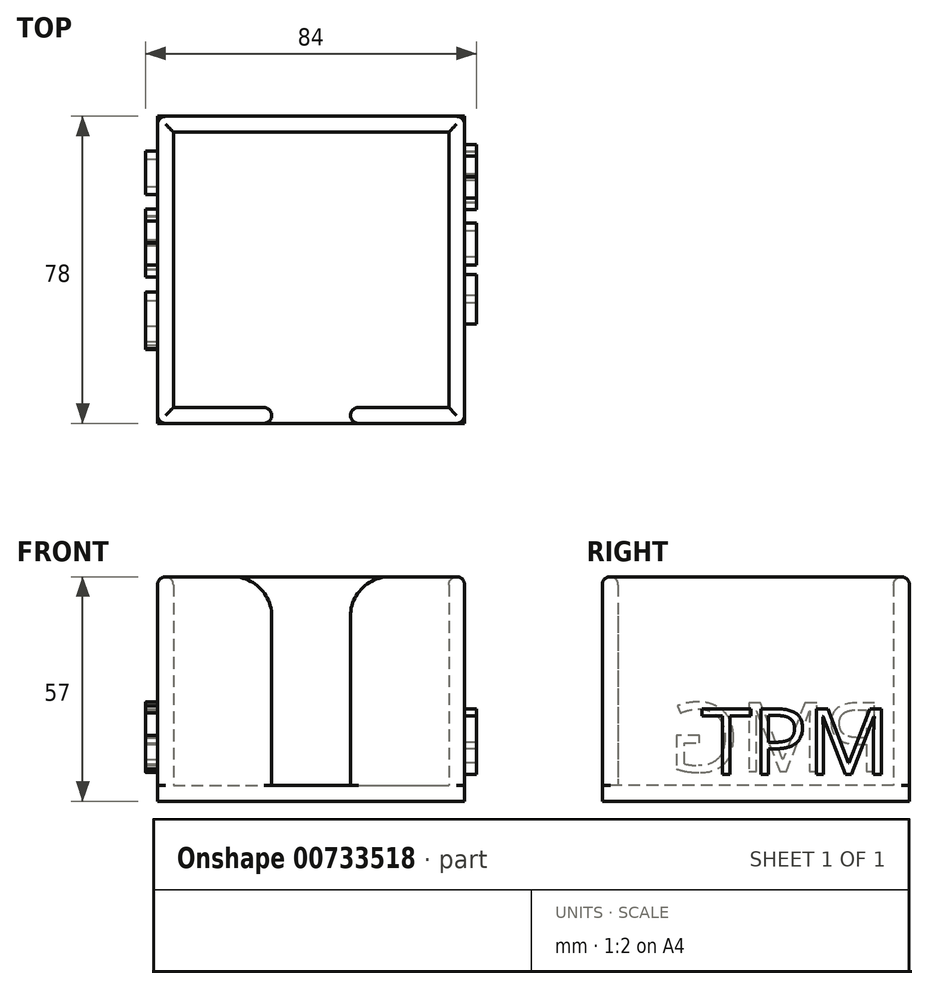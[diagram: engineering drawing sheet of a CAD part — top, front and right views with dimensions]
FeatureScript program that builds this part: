
annotation { "Feature Type Name" : "Feature", "Feature Type Description" : "" }
export const myFeature = defineFeature(function(context is Context, id is Id, definition is map)
    precondition{}
    {
        {
            var Q0;
            Q0=qCreatedBy(makeId("Top.planeOp"),FACE);
            var sketch = newSketch(context, id + "F0", { "sketchPlane" : qUnion([Q0])});
            skLineSegment(sketch, "E0.bottom", {"start": v(0, 0) * mm, "end": v(78, 0) * mm});
            skLineSegment(sketch, "E0.top", {"start": v(0, -78) * mm, "end": v(29, -78) * mm});
            skLineSegment(sketch, "E0.left", {"start": v(0, 0) * mm, "end": v(0, -78) * mm});
            skLineSegment(sketch, "E0.right", {"start": v(78, 0) * mm, "end": v(78, -78) * mm});
            skLineSegment(sketch, "E1.bottom", {"start": v(4, -4) * mm, "end": v(74, -4) * mm});
            skLineSegment(sketch, "E1.top", {"start": v(4, -74) * mm, "end": v(29, -74) * mm});
            skLineSegment(sketch, "E1.left", {"start": v(4, -4) * mm, "end": v(4, -74) * mm});
            skLineSegment(sketch, "E1.right", {"start": v(74, -4) * mm, "end": v(74, -74) * mm});
            skLineSegment(sketch, "E2", {"start": v(29, -74) * mm, "end": v(29, -78) * mm});
            skLineSegment(sketch, "E3", {"start": v(49, -74) * mm, "end": v(49, -78) * mm});
            skLineSegment(sketch, "E4.trimOffspring", {"start": v(49, -74) * mm, "end": v(74, -74) * mm});
            skLineSegment(sketch, "E5.trimOffspring", {"start": v(49, -78) * mm, "end": v(78, -78) * mm});
            skSolve(sketch);
        }
        {
            var Q0;
            Q0 = qSketchRegion(id + "F0", true);
            extrude(context, id + "F1", {"entities" : qUnion([Q0]), "depth" : 57 * mm, "offsetDistance" : 25 * mm});
        }
        {
            var Q0;
            Q0=makeQuery(id+"F1.opExtrude","CAP_EDGE",EDGE,{"disambiguationData":[OSD([sQuery(id+"F0.wireOp",EDGE,"E2")])],"isStart":false});
            var Q1;
            Q1=makeQuery(id+"F1.opExtrude","CAP_EDGE",EDGE,{"disambiguationData":[OSD([sQuery(id+"F0.wireOp",EDGE,"E3")])],"isStart":false});
            fillet(context, id + "F2", {"entities" : qUnion([Q0, Q1]), "radius" : 10 * mm, "tangentPropagation" : true, "allowEdgeOverflow" : false});
        }
        {
            var Q0;
            Q0=makeQuery(id+"F1.opExtrude","CAP_EDGE",EDGE,{"disambiguationData":[OSD([sQuery(id+"F0.wireOp",EDGE,"E0.top")])],"isStart":false});
            var Q1;
            Q1=makeQuery(id+"F1.opExtrude","CAP_EDGE",EDGE,{"disambiguationData":[OSD([sQuery(id+"F0.wireOp",EDGE,"E1.top")])],"isStart":false});
            var Q2;
            Q2=makeQuery(id+"F1.opExtrude","CAP_EDGE",EDGE,{"disambiguationData":[OSD([sQuery(id+"F0.wireOp",EDGE,"E1.left")])],"isStart":false});
            var Q3;
            Q3=makeQuery(id+"F1.opExtrude","CAP_EDGE",EDGE,{"disambiguationData":[OSD([sQuery(id+"F0.wireOp",EDGE,"E0.left")])],"isStart":false});
            var Q4;
            Q4=makeQuery(id+"F1.opExtrude","CAP_EDGE",EDGE,{"disambiguationData":[OSD([sQuery(id+"F0.wireOp",EDGE,"E1.bottom")])],"isStart":false});
            var Q5;
            Q5=makeQuery(id+"F1.opExtrude","CAP_EDGE",EDGE,{"disambiguationData":[OSD([sQuery(id+"F0.wireOp",EDGE,"E0.bottom")])],"isStart":false});
            var Q6;
            Q6=makeQuery(id+"F1.opExtrude","CAP_EDGE",EDGE,{"disambiguationData":[OSD([sQuery(id+"F0.wireOp",EDGE,"E0.right")])],"isStart":false});
            var Q7;
            Q7=makeQuery(id+"F1.opExtrude","CAP_EDGE",EDGE,{"disambiguationData":[OSD([sQuery(id+"F0.wireOp",EDGE,"E1.right")])],"isStart":false});
            var Q8;
            Q8=makeQuery(id+"F1.opExtrude","CAP_EDGE",EDGE,{"disambiguationData":[OSD([sQuery(id+"F0.wireOp",EDGE,"E4.trimOffspring")])],"isStart":false});
            var Q9;
            Q9=makeQuery(id+"F1.opExtrude","CAP_EDGE",EDGE,{"disambiguationData":[OSD([sQuery(id+"F0.wireOp",EDGE,"E5.trimOffspring")])],"isStart":false});
            var Q10;
            Q10=makeQuery(id+"F1.opExtrude","SWEPT_EDGE",EDGE,{"disambiguationData":[OSD([sQuery(id+"F0.wireOp",EDGE,"E0.top"),sQuery(id+"F0.wireOp",EDGE,"E0.left")])]});
            var Q11;
            Q11=makeQuery(id+"F1.opExtrude","SWEPT_EDGE",EDGE,{"disambiguationData":[OSD([sQuery(id+"F0.wireOp",EDGE,"E0.bottom"),sQuery(id+"F0.wireOp",EDGE,"E0.right")])]});
            var Q12;
            Q12=makeQuery(id+"F1.opExtrude","SWEPT_EDGE",EDGE,{"disambiguationData":[OSD([sQuery(id+"F0.wireOp",EDGE,"E0.right"),sQuery(id+"F0.wireOp",EDGE,"E5.trimOffspring")])]});
            var Q13;
            Q13=makeQuery(id+"F1.opExtrude","SWEPT_EDGE",EDGE,{"disambiguationData":[OSD([sQuery(id+"F0.wireOp",EDGE,"E0.bottom"),sQuery(id+"F0.wireOp",EDGE,"E0.left")])]});
            fillet(context, id + "F3", {"entities" : qUnion([Q0, Q1, Q2, Q3, Q4, Q5, Q6, Q7, Q8, Q9, Q10, Q11, Q12, Q13]), "radius" : 2 * mm, "tangentPropagation" : true, "allowEdgeOverflow" : false});
        }
        {
            var Q0;
            Q0=qCreatedBy(makeId("Top.planeOp"),FACE);
            var sketch = newSketch(context, id + "F4", { "sketchPlane" : qUnion([Q0])});
            skLineSegment(sketch, "E6.bottom", {"start": v(0, 0) * mm, "end": v(78, 0) * mm});
            skLineSegment(sketch, "E6.top", {"start": v(0, -78) * mm, "end": v(78, -78) * mm});
            skLineSegment(sketch, "E6.left", {"start": v(0, 0) * mm, "end": v(0, -78) * mm});
            skLineSegment(sketch, "E6.right", {"start": v(78, 0) * mm, "end": v(78, -78) * mm});
            skSolve(sketch);
        }
        {
            var Q0;
            Q0 = qSketchRegion(id + "F4", true);
            extrude(context, id + "F5", {"entities" : qUnion([Q0]), "operationType" : NewBodyOperationType.ADD, "depth" : 4 * mm, "offsetDistance" : 25 * mm});
        }
        {
            var Q0;
            Q0=makeQuery(id+"F5.boolean.opBoolean","MERGE",FACE,{"derivedFrom":[makeQuery(id+"F1.opExtrude","SWEPT_FACE",FACE,{"disambiguationData":[OSD([sQuery(id+"F0.wireOp",EDGE,"E0.right")])]}),makeQuery(id+"F5.opExtrude","SWEPT_FACE",FACE,{"disambiguationData":[OSD([sQuery(id+"F4.wireOp",EDGE,"E6.right")])]})]});
            var sketch = newSketch(context, id + "F6", { "sketchPlane" : qUnion([Q0])});
            skText(sketch, "E7", { "text": "TPM", "fontName": "OpenSans-Regular.ttf"});
            const initialGuessF6  = {"E7": [-0.05296, 0.00675, 1, 0, 0.01683]};
            skSetInitialGuess(sketch, initialGuessF6);
            skSolve(sketch);
        }
        {
            var Q0;
            Q0 = qSketchRegion(id + "F6", true);
            extrude(context, id + "F7", {"entities" : qUnion([Q0]), "operationType" : NewBodyOperationType.ADD, "depth" : 3 * mm, "offsetDistance" : 25 * mm});
        }
        {
            var Q0;
            Q0=makeQuery(id+"F5.boolean.opBoolean","MERGE",FACE,{"derivedFrom":[makeQuery(id+"F1.opExtrude","SWEPT_FACE",FACE,{"disambiguationData":[OSD([sQuery(id+"F0.wireOp",EDGE,"E0.left")])]}),makeQuery(id+"F5.opExtrude","SWEPT_FACE",FACE,{"disambiguationData":[OSD([sQuery(id+"F4.wireOp",EDGE,"E6.left")])]})]});
            var sketch = newSketch(context, id + "F8", { "sketchPlane" : qUnion([Q0])});
            skText(sketch, "E8", { "text": "PMG", "fontName": "OpenSans-Regular.ttf"});
            const initialGuessF8  = {"E8": [0.00642, 0.00751, 1, 0, 0.0176]};
            skSetInitialGuess(sketch, initialGuessF8);
            skSolve(sketch);
        }
        {
            var Q0;
            Q0 = qSketchRegion(id + "F8", true);
            extrude(context, id + "F9", {"entities" : qUnion([Q0]), "operationType" : NewBodyOperationType.ADD, "depth" : 3 * mm, "offsetDistance" : 25 * mm});
        }
    });
